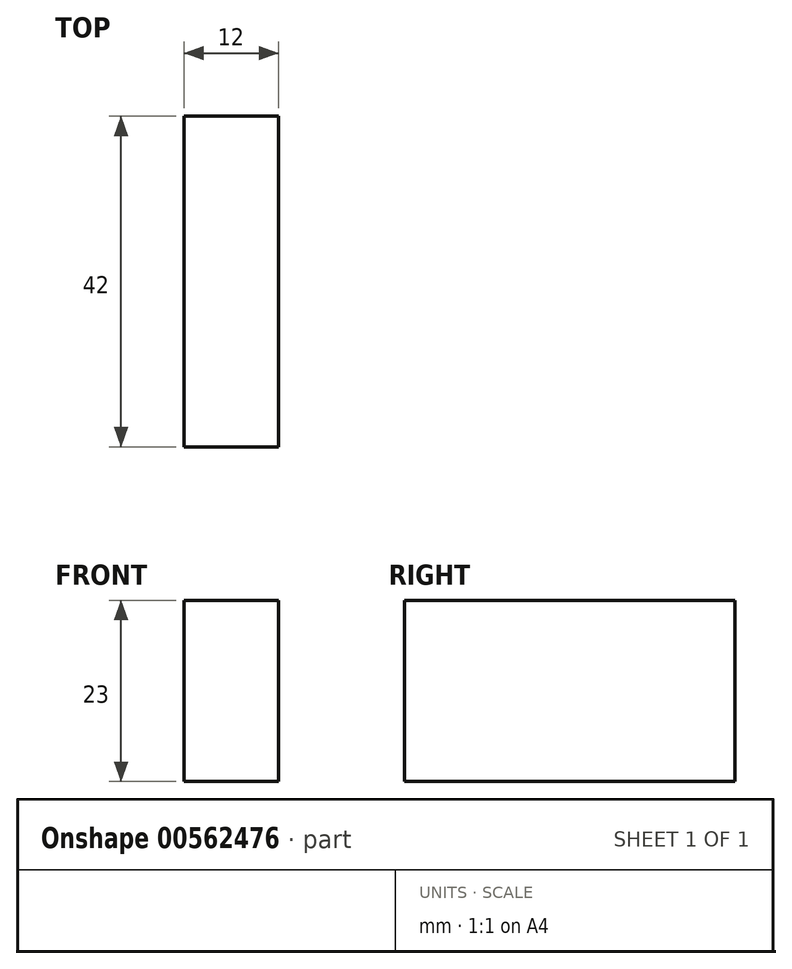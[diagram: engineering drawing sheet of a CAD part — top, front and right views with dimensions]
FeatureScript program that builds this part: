
annotation { "Feature Type Name" : "Feature", "Feature Type Description" : "" }
export const myFeature = defineFeature(function(context is Context, id is Id, definition is map)
    precondition{}
    {
        {
            var Q0;
            Q0=qCreatedBy(makeId("Right.planeOp"),FACE);
            var sketch = newSketch(context, id + "F0", { "sketchPlane" : qUnion([Q0])});
            skLineSegment(sketch, "E0.bottom", {"start": v(-21, 11.5) * mm, "end": v(21, 11.5) * mm});
            skLineSegment(sketch, "E0.top", {"start": v(-21, -11.5) * mm, "end": v(21, -11.5) * mm});
            skLineSegment(sketch, "E0.left", {"start": v(-21, 11.5) * mm, "end": v(-21, -11.5) * mm});
            skLineSegment(sketch, "E0.right", {"start": v(21, 11.5) * mm, "end": v(21, -11.5) * mm});
            skPoint(sketch, "E0.middle", {"position": v(0, 0) * mm});
            skSolve(sketch);
        }
        {
            var Q0;
            Q0=makeQuery(id+"F0.imprint","IMPRINT",FACE,{"disambiguationData":[TD([[makeQuery(id+"F0.imprint","IMPRINT",EDGE,{"derivedFrom":sQuery(id+"F0.wireOp",EDGE,"E0.bottom")}),-1.0]])]});
            extrude(context, id + "F1", {"entities" : qUnion([Q0]), "depth" : 12 * mm, "offsetDistance" : 25 * mm, "symmetric" : true});
        }
    });
